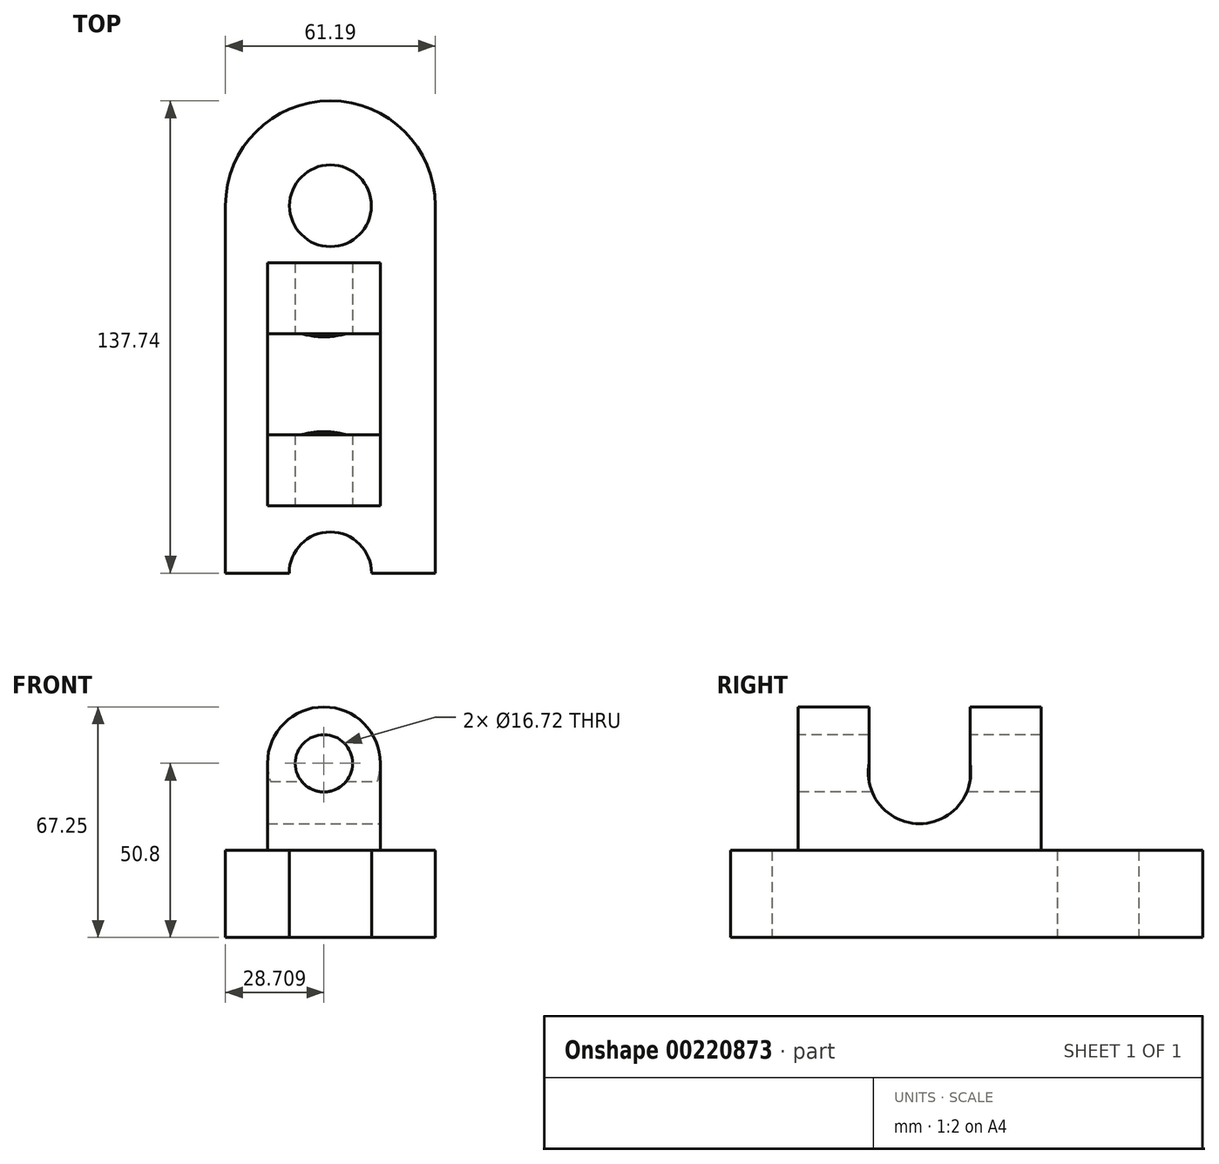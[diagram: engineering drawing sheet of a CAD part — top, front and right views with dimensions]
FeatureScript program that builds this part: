
annotation { "Feature Type Name" : "Feature", "Feature Type Description" : "" }
export const myFeature = defineFeature(function(context is Context, id is Id, definition is map)
    precondition{}
    {
        {
            var Q0;
            Q0=qCreatedBy(makeId("Top.planeOp"),FACE);
            var sketch = newSketch(context, id + "F0", { "sketchPlane" : qUnion([Q0])});
            skLineSegment(sketch, "E0.bottom", {"start": v(-32.79, 53) * mm, "end": v(28.4, 53) * mm});
            skLineSegment(sketch, "E0.top", {"start": v(-32.79, -54.15) * mm, "end": v(28.4, -54.15) * mm});
            skLineSegment(sketch, "E0.left", {"start": v(-32.79, 53) * mm, "end": v(-32.79, -54.15) * mm});
            skLineSegment(sketch, "E0.right", {"start": v(28.4, 53) * mm, "end": v(28.4, -54.15) * mm});
            skArc(sketch, "E1", {"start": v(28.4, 53) * mm, "mid": v(-2.2, 83.59) * mm, "end": v(-32.79, 53) * mm});
            skArc(sketch, "E2", {"start": v(28.4, -54.15) * mm, "mid": v(-2.2, -84.74) * mm, "end": v(-32.79, -54.15) * mm});
            skCircle(sketch, "E3", {"center": v(-2.2, 53) * mm, "radius": 11.91 * mm});
            skCircle(sketch, "E4", {"center": v(-2.2, -54.15) * mm, "radius": 12.03 * mm});
            skLineSegment(sketch, "E5.bottom", {"start": v(-20.53, -34.5) * mm, "end": v(12.37, -34.5) * mm});
            skLineSegment(sketch, "E5.top", {"start": v(-20.53, 36.4) * mm, "end": v(12.37, 36.4) * mm});
            skLineSegment(sketch, "E5.left", {"start": v(-20.53, -34.5) * mm, "end": v(-20.53, 36.4) * mm});
            skLineSegment(sketch, "E5.right", {"start": v(12.37, -34.5) * mm, "end": v(12.37, 36.4) * mm});
            skSolve(sketch);
        }
        {
            var Q0;
            {var subQ6=sQuery(id+"F0.wireOp",EDGE,"E0.left");Q0=makeQuery(id+"F0.imprint","IMPRINT",FACE,{"disambiguationData":[TD([[makeQuery(id+"F0.imprint","IMPRINT",EDGE,{"derivedFrom":subQ6}),1.0]])]});}
            var Q1;
            {var subQ0=sQuery(id+"F0.wireOp",EDGE,"E1");Q1=makeQuery(id+"F0.imprint","IMPRINT",FACE,{"disambiguationData":[TD([[makeQuery(id+"F0.imprint","IMPRINT",EDGE,{"derivedFrom":subQ0}),1.0]])]});}
            var Q2;
            {var subQ0=sQuery(id+"F0.wireOp",EDGE,"E2");Q2=makeQuery(id+"F0.imprint","IMPRINT",FACE,{"disambiguationData":[TD([[makeQuery(id+"F0.imprint","IMPRINT",EDGE,{"derivedFrom":subQ0}),-1.0]])]});}
            extrude(context, id + "F1", {"entities" : qUnion([Q0, Q1, Q2]), "depth" : 25.4 * mm});
        }
        {
            var Q0;
            Q0=makeQuery(id+"F0.imprint","IMPRINT",FACE,{"disambiguationData":[TD([[makeQuery(id+"F0.imprint","IMPRINT",EDGE,{"derivedFrom":sQuery(id+"F0.wireOp",EDGE,"E5.bottom")}),1.0]])]});
            extrude(context, id + "F2", {"entities" : qUnion([Q0]), "operationType" : NewBodyOperationType.ADD, "depth" : 50.8 * mm});
        }
        {
            var Q0;
            Q0=makeQuery(id+"F2.opExtrude","SWEPT_FACE",FACE,{"disambiguationData":[OSD([sQuery(id+"F0.wireOp",EDGE,"E5.right")])]});
            var sketch = newSketch(context, id + "F3", { "sketchPlane" : qUnion([Q0])});
            skCircle(sketch, "E6", {"center": v(0.95, 48.14) * mm, "radius": 14.94 * mm});
            skPoint(sketch, "E6.centerSnap0", {"position": v(0.95, 50.8) * mm});
            skSolve(sketch);
        }
        {
            var Q0;
            Q0 = qSketchRegion(id + "F3", true);
            extrude(context, id + "F4", {"entities" : qUnion([Q0]), "operationType" : NewBodyOperationType.REMOVE, "oppositeDirection" : true, "depth" : 76.2 * mm});
        }
        {
            var Q0;
            {var subQ0=sQuery(id+"F0.wireOp",EDGE,"E5.top");var subQ1=sQuery(id+"F0.wireOp",EDGE,"E5.left");var subQ2=sQuery(id+"F0.wireOp",EDGE,"E5.right");Q0=makeQuery(id+"F4.boolean.opBoolean","SPLIT",FACE,{"disambiguationData":[TD([makeQuery(id+"F2.opExtrude","SWEPT_FACE",FACE,{"disambiguationData":[OSD([subQ0])]})])],"derivedFrom":makeQuery(id+"F2.opExtrude","CAP_FACE",FACE,{"disambiguationData":[OSD([sQuery(id+"F0.wireOp",EDGE,"E5.bottom"),subQ0,subQ1,subQ2])],"isStart":false})});}
            var sketch = newSketch(context, id + "F5", { "sketchPlane" : qUnion([Q0])});
            skLineSegment(sketch, "E7.bottom", {"start": v(-4.08, 36.4) * mm, "end": v(12.37, 36.4) * mm});
            skLineSegment(sketch, "E7.top", {"start": v(-4.08, 15.66) * mm, "end": v(12.37, 15.66) * mm});
            skLineSegment(sketch, "E7.left", {"start": v(-4.08, 36.4) * mm, "end": v(-4.08, 15.66) * mm});
            skLineSegment(sketch, "E7.right", {"start": v(12.37, 36.4) * mm, "end": v(12.37, 15.66) * mm});
            skSolve(sketch);
        }
        {
            var Q0;
            Q0=makeQuery(id+"F5.imprint","IMPRINT",FACE,{"disambiguationData":[TD([[makeQuery(id+"F5.imprint","IMPRINT",EDGE,{"derivedFrom":sQuery(id+"F5.wireOp",EDGE,"E7.bottom")}),-1.0]])]});
            var Q1;
            Q1=sQuery(id+"F5.wireOp",EDGE,"E7.left");
            revolve(context, id + "F6", {"operationType" : NewBodyOperationType.ADD, "entities" : qUnion([Q0]), "axis" : qUnion([Q1]), "revolveType" : RevolveType.FULL});
        }
        {
            var Q0;
            {var subQ0=sQuery(id+"F0.wireOp",EDGE,"E5.bottom");var subQ1=sQuery(id+"F0.wireOp",EDGE,"E5.left");var subQ2=sQuery(id+"F0.wireOp",EDGE,"E5.right");Q0=makeQuery(id+"F4.boolean.opBoolean","SPLIT",FACE,{"disambiguationData":[TD([makeQuery(id+"F2.opExtrude","SWEPT_FACE",FACE,{"disambiguationData":[OSD([subQ0])]})])],"derivedFrom":makeQuery(id+"F2.opExtrude","CAP_FACE",FACE,{"disambiguationData":[OSD([subQ0,sQuery(id+"F0.wireOp",EDGE,"E5.top"),subQ1,subQ2])],"isStart":false})});}
            var sketch = newSketch(context, id + "F7", { "sketchPlane" : qUnion([Q0])});
            skLineSegment(sketch, "E8.bottom", {"start": v(-4.08, -34.5) * mm, "end": v(-20.53, -34.5) * mm});
            skLineSegment(sketch, "E8.top", {"start": v(-4.08, -13.75) * mm, "end": v(-20.53, -13.75) * mm});
            skLineSegment(sketch, "E8.left", {"start": v(-4.08, -34.5) * mm, "end": v(-4.08, -13.75) * mm});
            skLineSegment(sketch, "E8.right", {"start": v(-20.53, -34.5) * mm, "end": v(-20.53, -13.75) * mm});
            skSolve(sketch);
        }
        {
            var Q0;
            Q0=makeQuery(id+"F7.imprint","IMPRINT",FACE,{"disambiguationData":[TD([[makeQuery(id+"F7.imprint","IMPRINT",EDGE,{"derivedFrom":sQuery(id+"F7.wireOp",EDGE,"E8.bottom")}),1.0]])]});
            var Q1;
            Q1=sQuery(id+"F7.wireOp",EDGE,"E8.left");
            revolve(context, id + "F8", {"operationType" : NewBodyOperationType.ADD, "entities" : qUnion([Q0]), "axis" : qUnion([Q1]), "revolveType" : RevolveType.FULL});
        }
        {
            var Q0;
            Q0=makeQuery(id+"F8.boolean.opBoolean","MERGE",FACE,{"derivedFrom":[makeQuery(id+"F2.opExtrude","SWEPT_FACE",FACE,{"disambiguationData":[OSD([sQuery(id+"F0.wireOp",EDGE,"E5.bottom")])]}),makeQuery(id+"F8.opRevolve","SWEPT_FACE",FACE,{"disambiguationData":[OSD([sQuery(id+"F7.wireOp",EDGE,"E8.bottom")])]})]});
            var sketch = newSketch(context, id + "F9", { "sketchPlane" : qUnion([Q0])});
            skCircle(sketch, "E9", {"center": v(-4.08, 50.8) * mm, "radius": 8.36 * mm});
            skSolve(sketch);
        }
        {
            var Q0;
            Q0=makeQuery(id+"F9.imprint","IMPRINT",FACE,{"disambiguationData":[TD([[makeQuery(id+"F9.imprint","IMPRINT",EDGE,{"derivedFrom":sQuery(id+"F9.wireOp",EDGE,"E9")}),1.0]])]});
            extrude(context, id + "F10", {"entities" : qUnion([Q0]), "operationType" : NewBodyOperationType.REMOVE, "oppositeDirection" : true, "depth" : 508 * mm});
        }
    });
